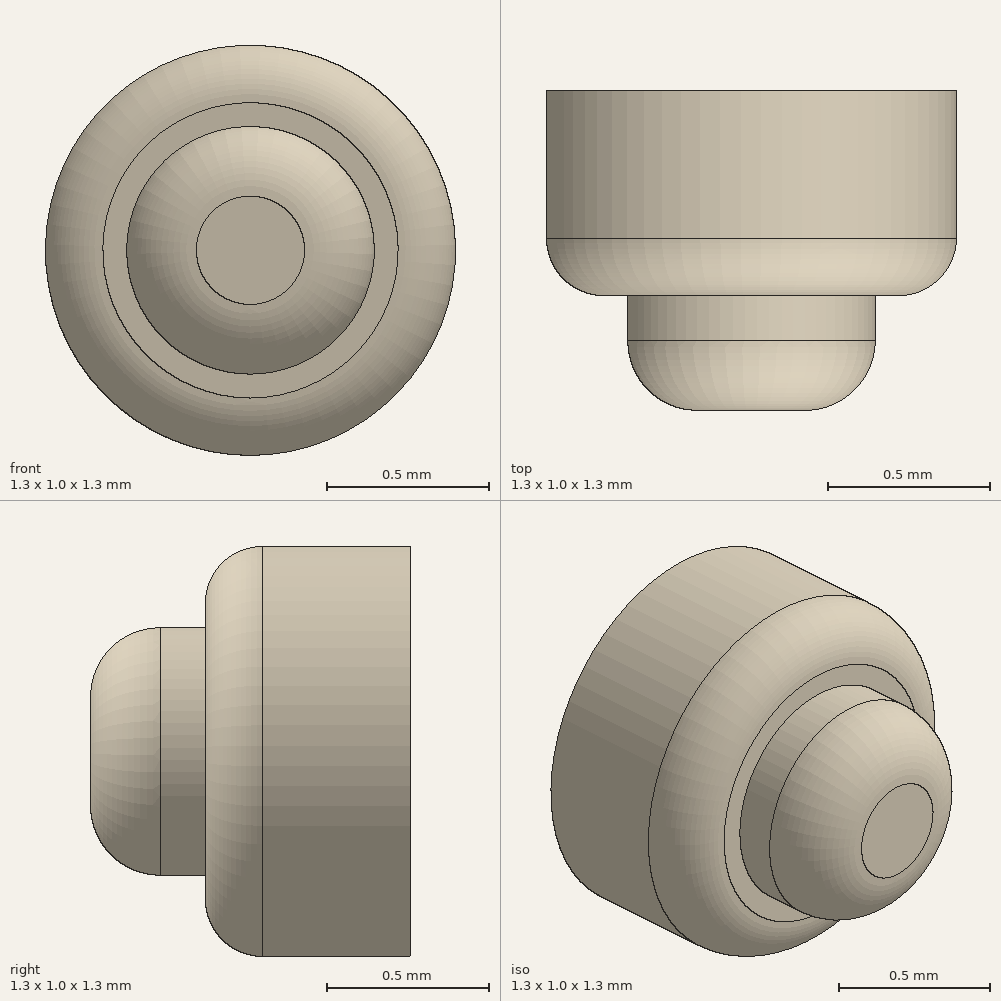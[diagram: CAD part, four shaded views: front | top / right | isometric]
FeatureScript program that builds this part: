
annotation { "Feature Type Name" : "Feature", "Feature Type Description" : "" }
export const myFeature = defineFeature(function(context is Context, id is Id, definition is map)
    precondition{}
    {
        {
            var Q0;
            Q0=qCreatedBy(makeId("Front.planeOp"),FACE);
            var sketch = newSketch(context, id + "F0", { "sketchPlane" : qUnion([Q0])});
            skCircle(sketch, "E0", {"center": v(-56.25, 38.7) * mm, "radius": 0.64 * mm});
            skSolve(sketch);
        }
        {
            var Q0;
            Q0=makeQuery(id+"F0.imprint","IMPRINT",FACE,{"disambiguationData":[TD([[makeQuery(id+"F0.imprint","IMPRINT",EDGE,{"derivedFrom":sQuery(id+"F0.wireOp",EDGE,"E0")}),1.0]])]});
            extrude(context, id + "F1", {"entities" : qUnion([Q0]), "depth" : 0.64 * mm});
        }
        {
            var Q0;
            Q0=makeQuery(id+"F1.opExtrude","CAP_FACE",FACE,{"disambiguationData":[OSD([sQuery(id+"F0.wireOp",EDGE,"E0")])],"isStart":false});
            var sketch = newSketch(context, id + "F2", { "sketchPlane" : qUnion([Q0])});
            skCircle(sketch, "E1", {"center": v(-56.25, 38.7) * mm, "radius": 0.38 * mm});
            skSolve(sketch);
        }
        {
            var Q0;
            Q0=makeQuery(id+"F2.imprint","IMPRINT",FACE,{"disambiguationData":[TD([[makeQuery(id+"F2.imprint","IMPRINT",EDGE,{"derivedFrom":sQuery(id+"F2.wireOp",EDGE,"E1")}),1.0]])]});
            extrude(context, id + "F3", {"entities" : qUnion([Q0]), "operationType" : NewBodyOperationType.ADD, "depth" : 0.36 * mm});
        }
        {
            var Q0;
            Q0=makeQuery(id+"F1.opExtrude","CAP_EDGE",EDGE,{"disambiguationData":[OSD([sQuery(id+"F0.wireOp",EDGE,"E0")])],"isStart":false});
            fillet(context, id + "F4", {"entities" : qUnion([Q0]), "radius" : 0.18 * mm, "tangentPropagation" : true, "allowEdgeOverflow" : false});
        }
        {
            var Q0;
            Q0=makeQuery(id+"F3.opExtrude","CAP_EDGE",EDGE,{"disambiguationData":[OSD([sQuery(id+"F2.wireOp",EDGE,"E1")])],"isStart":false});
            fillet(context, id + "F5", {"entities" : qUnion([Q0]), "radius" : 0.22 * mm, "tangentPropagation" : true, "allowEdgeOverflow" : false});
        }
    });
